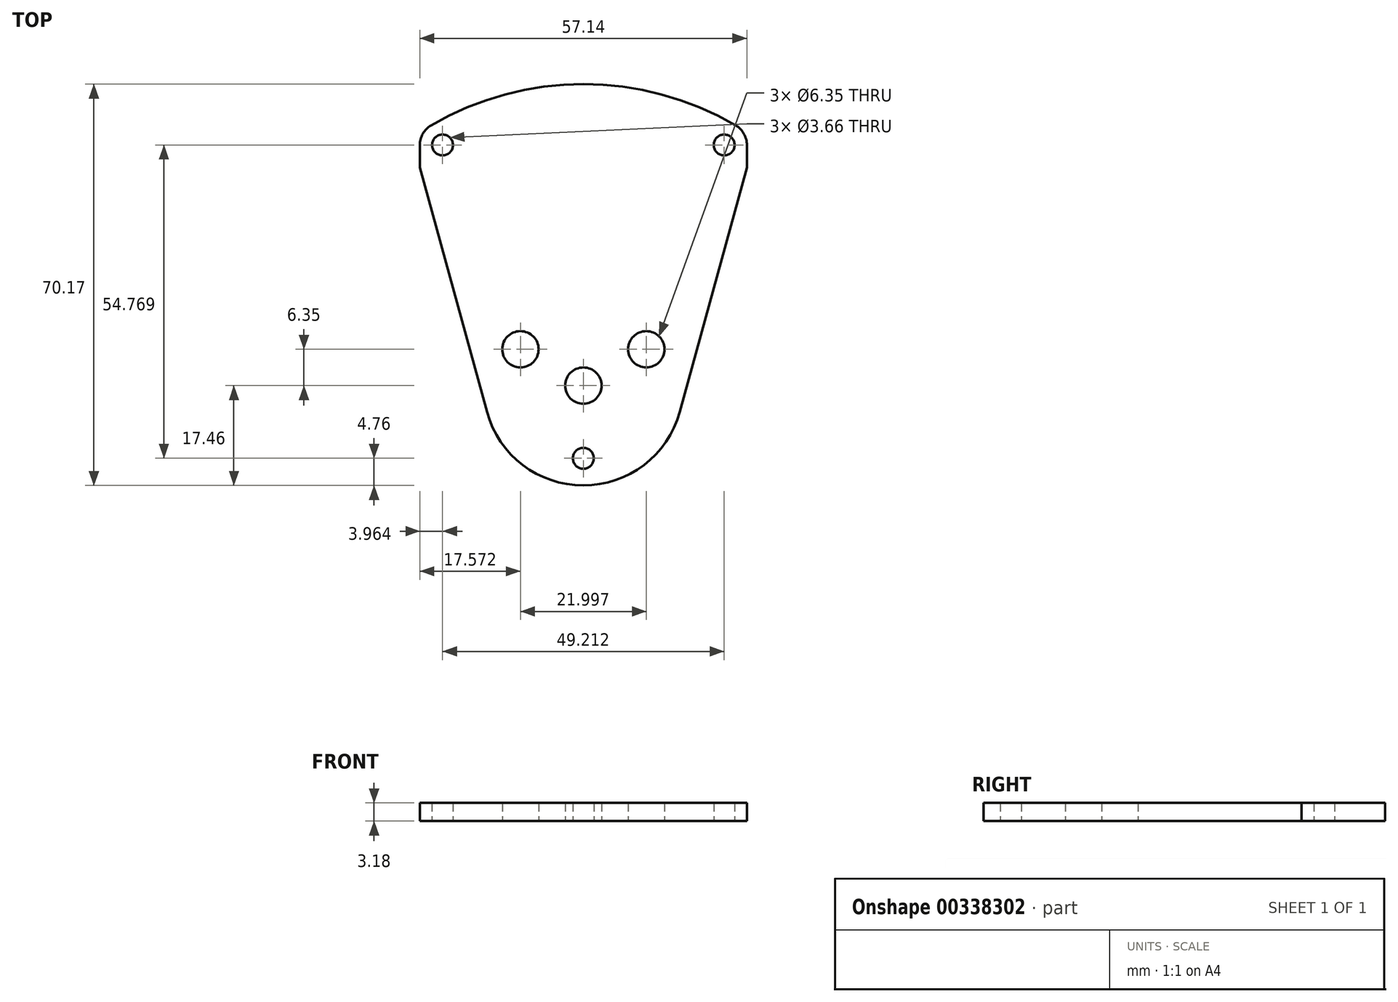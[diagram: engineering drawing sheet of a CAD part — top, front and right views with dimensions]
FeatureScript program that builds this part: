
annotation { "Feature Type Name" : "Feature", "Feature Type Description" : "" }
export const myFeature = defineFeature(function(context is Context, id is Id, definition is map)
    precondition{}
    {
        {
            var Q0;
            Q0=qCreatedBy(makeId("Top.planeOp"),FACE);
            var sketch = newSketch(context, id + "F0", { "sketchPlane" : qUnion([Q0])});
            skCircle(sketch, "E0", {"center": v(0, -38.1) * mm, "radius": 3.18 * mm});
            skArc(sketch, "E1", {"start": v(-16.84, -42.73) * mm, "mid": v(0, -55.56) * mm, "end": v(16.84, -42.73) * mm});
            skLineSegment(sketch, "E2", {"start": v(-11, -31.75) * mm, "end": v(11, -31.75) * mm, "construction": true});
            skCircle(sketch, "E3", {"center": v(11, -31.75) * mm, "radius": 3.18 * mm});
            skCircle(sketch, "E4", {"center": v(-11, -31.75) * mm, "radius": 3.18 * mm});
            skLineSegment(sketch, "E5", {"start": v(0, -38.1) * mm, "end": v(0, -50.8) * mm, "construction": true});
            skCircle(sketch, "E6", {"center": v(0, -50.8) * mm, "radius": 1.83 * mm});
            skLineSegment(sketch, "E7", {"start": v(-28.57, 0) * mm, "end": v(-28.57, 3.97) * mm});
            skLineSegment(sketch, "E8", {"start": v(28.58, 0) * mm, "end": v(28.58, 3.97) * mm});
            skLineSegment(sketch, "E9", {"start": v(16.84, -42.73) * mm, "end": v(28.57, 0) * mm});
            skLineSegment(sketch, "E10", {"start": v(-16.84, -42.73) * mm, "end": v(-28.57, 0) * mm});
            skLineSegment(sketch, "E11", {"start": v(0, -38.1) * mm, "end": v(-11, -31.75) * mm, "construction": true});
            skLineSegment(sketch, "E12", {"start": v(11, -31.75) * mm, "end": v(0, -38.1) * mm, "construction": true});
            skLineSegment(sketch, "E13", {"start": v(-28.57, 0) * mm, "end": v(28.57, 0) * mm, "construction": true});
            skLineSegment(sketch, "E14", {"start": v(0, -38.1) * mm, "end": v(0, 0) * mm, "construction": true});
            skPoint(sketch, "E14.endSnap0", {"position": v(0, -31.75) * mm});
            skCircle(sketch, "E15", {"center": v(0, -50.8) * mm, "radius": 4.76 * mm, "construction": true});
            skLineSegment(sketch, "E16", {"start": v(-11, -31.75) * mm, "end": v(0, -50.8) * mm, "construction": true});
            skLineSegment(sketch, "E17", {"start": v(11, -31.75) * mm, "end": v(0, -50.8) * mm, "construction": true});
            skArc(sketch, "E18", {"start": v(-26.61, 7.4) * mm, "mid": v(-28.05, 5.94) * mm, "end": v(-28.57, 3.97) * mm});
            skArc(sketch, "E19", {"start": v(28.57, 3.97) * mm, "mid": v(28.05, 5.94) * mm, "end": v(26.61, 7.4) * mm});
            skArc(sketch, "E20", {"start": v(26.61, 7.4) * mm, "mid": v(0, 14.6) * mm, "end": v(-26.61, 7.4) * mm});
            skLineSegment(sketch, "E21", {"start": v(0, 0) * mm, "end": v(0, 14.6) * mm, "construction": true});
            skArc(sketch, "E22", {"start": v(-26.61, 7.4) * mm, "mid": v(0, -90.8) * mm, "end": v(26.61, 7.4) * mm, "construction": true});
            skCircle(sketch, "E23", {"center": v(24.6, 3.97) * mm, "radius": 1.83 * mm});
            skCircle(sketch, "E24", {"center": v(-24.6, 3.97) * mm, "radius": 1.83 * mm});
            skSolve(sketch);
        }
        {
            var Q0;
            Q0=qSketchRegion(id+"F0",true);
            extrude(context, id + "F1", {"entities" : qUnion([Q0]), "depth" : 3.17 * mm});
        }
    });
